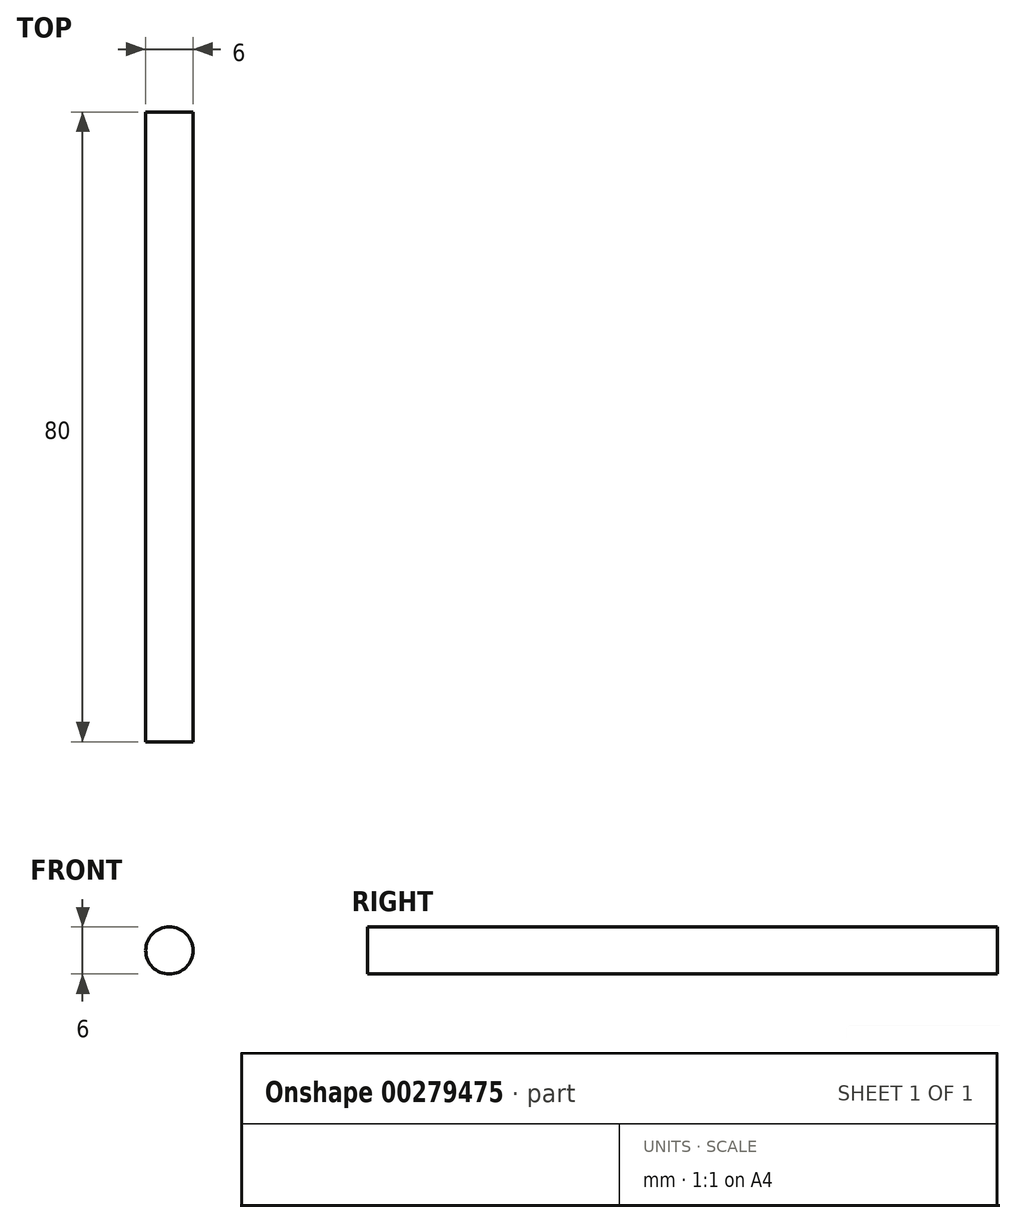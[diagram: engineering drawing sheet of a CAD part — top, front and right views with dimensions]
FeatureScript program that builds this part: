
annotation { "Feature Type Name" : "Feature", "Feature Type Description" : "" }
export const myFeature = defineFeature(function(context is Context, id is Id, definition is map)
    precondition{}
    {
        {
            var Q0;
            Q0=qCreatedBy(makeId("Front.planeOp"),FACE);
            var sketch = newSketch(context, id + "F0", { "sketchPlane" : qUnion([Q0])});
            skCircle(sketch, "E0", {"center": v(-22.2, 11.55) * mm, "radius": 3 * mm});
            skSolve(sketch);
        }
        {
            var Q0;
            Q0=makeQuery(id+"F0.imprint","IMPRINT",FACE,{"disambiguationData":[TD([[makeQuery(id+"F0.imprint","IMPRINT",EDGE,{"derivedFrom":sQuery(id+"F0.wireOp",EDGE,"E0")}),1.0]])]});
            extrude(context, id + "F1", {"entities" : qUnion([Q0]), "depth" : 80 * mm});
        }
    });
